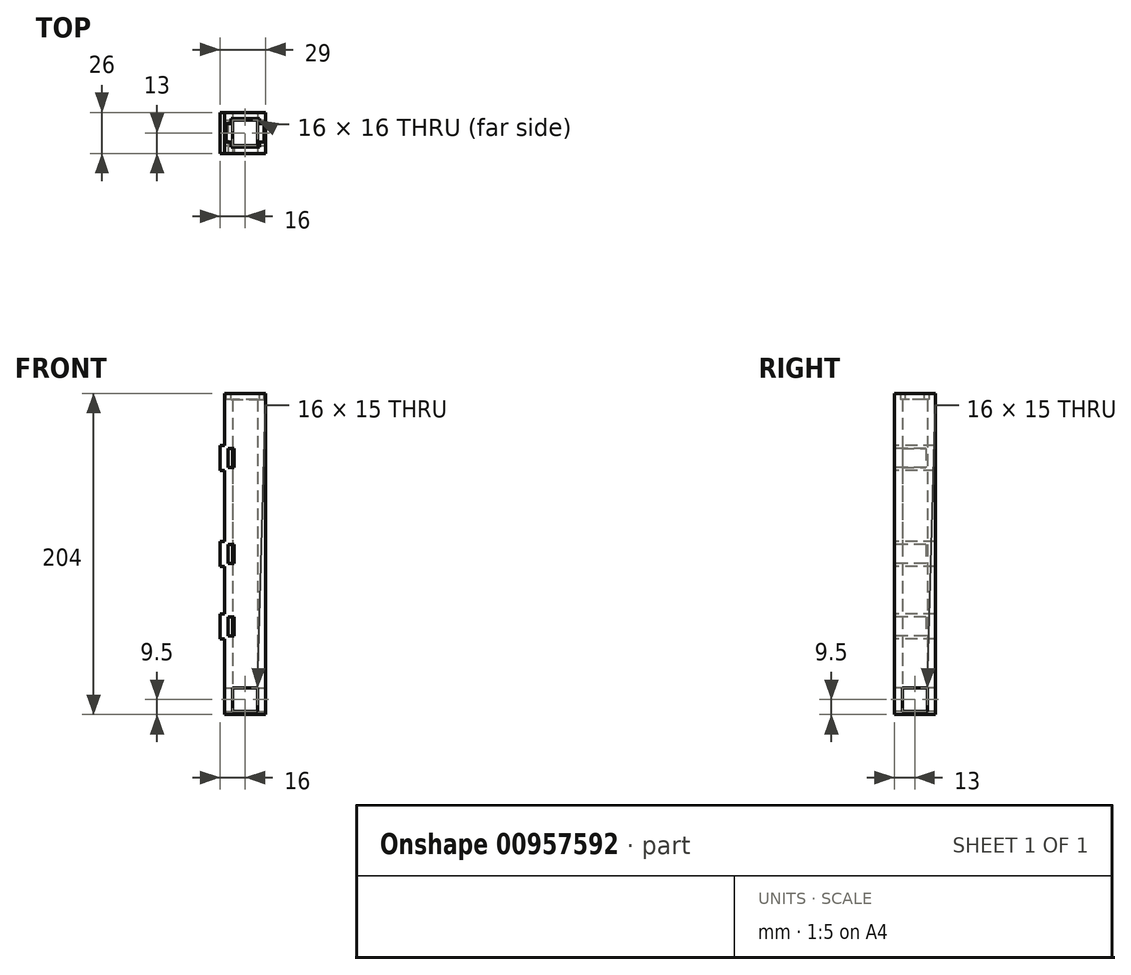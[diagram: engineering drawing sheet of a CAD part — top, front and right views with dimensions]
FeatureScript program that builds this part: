
annotation { "Feature Type Name" : "Feature", "Feature Type Description" : "" }
export const myFeature = defineFeature(function(context is Context, id is Id, definition is map)
    precondition{}
    {
        {
            var Q0;
            Q0=qCreatedBy(makeId("Top.planeOp"),FACE);
            var sketch = newSketch(context, id + "F0", { "sketchPlane" : qUnion([Q0])});
            skLineSegment(sketch, "E0.bottom", {"start": v(13, 13) * mm, "end": v(-13, 13) * mm});
            skLineSegment(sketch, "E0.top", {"start": v(13, -13) * mm, "end": v(-13, -13) * mm});
            skLineSegment(sketch, "E0.left", {"start": v(13, 13) * mm, "end": v(13, -13) * mm});
            skLineSegment(sketch, "E0.right", {"start": v(-13, 13) * mm, "end": v(-13, -13) * mm});
            skPoint(sketch, "E0.middle", {"position": v(0, 0) * mm});
            skLineSegment(sketch, "E1.bottom", {"start": v(8, 8) * mm, "end": v(-8, 8) * mm});
            skLineSegment(sketch, "E1.top", {"start": v(8, -8) * mm, "end": v(-8, -8) * mm});
            skLineSegment(sketch, "E1.left", {"start": v(8, 8) * mm, "end": v(8, -8) * mm});
            skLineSegment(sketch, "E1.right", {"start": v(-8, 8) * mm, "end": v(-8, -8) * mm});
            skSolve(sketch);
        }
        {
            var Q0;
            Q0=makeQuery(id+"F0.imprint","IMPRINT",FACE,{"disambiguationData":[TD([[makeQuery(id+"F0.imprint","IMPRINT",EDGE,{"derivedFrom":sQuery(id+"F0.wireOp",EDGE,"E0.bottom")}),1.0]])]});
            var Q1;
            Q1=makeQuery(id+"F0.imprint","IMPRINT",FACE,{"disambiguationData":[TD([[makeQuery(id+"F0.imprint","IMPRINT",EDGE,{"derivedFrom":sQuery(id+"F0.wireOp",EDGE,"E1.bottom")}),-1.0]])]});
            var Q2;
            Q2=makeQuery(id+"F0.imprint","IMPRINT",FACE,{"disambiguationData":[TD([[makeQuery(id+"F0.imprint","IMPRINT",EDGE,{"derivedFrom":sQuery(id+"F0.wireOp",EDGE,"E1.bottom")}),1.0]])]});
            extrude(context, id + "F1", {"entities" : qUnion([Q0, Q1, Q2]), "depth" : 2 * mm, "offsetDistance" : 25 * mm});
        }
        {
            var Q0;
            Q0=qSketchRegion(id+"F0",true);
            var Q1;
            Q1=makeQuery(id+"F0.imprint","IMPRINT",FACE,{"disambiguationData":[TD([[makeQuery(id+"F0.imprint","IMPRINT",EDGE,{"derivedFrom":sQuery(id+"F0.wireOp",EDGE,"E1.bottom")}),-1.0]])]});
            extrude(context, id + "F2", {"entities" : qUnion([Q0, Q1]), "operationType" : NewBodyOperationType.ADD, "depth" : 200 * mm, "offsetDistance" : 25 * mm});
        }
        {
            var Q0;
            Q0=makeQuery(id+"F2.opExtrude","CAP_FACE",FACE,{"disambiguationData":[OSD([sQuery(id+"F0.wireOp",EDGE,"E0.bottom"),sQuery(id+"F0.wireOp",EDGE,"E0.top"),sQuery(id+"F0.wireOp",EDGE,"E0.left"),sQuery(id+"F0.wireOp",EDGE,"E0.right"),sQuery(id+"F0.wireOp",EDGE,"E1.bottom"),sQuery(id+"F0.wireOp",EDGE,"E1.top"),sQuery(id+"F0.wireOp",EDGE,"E1.left"),sQuery(id+"F0.wireOp",EDGE,"E1.right")])],"isStart":false});
            var sketch = newSketch(context, id + "F3", { "sketchPlane" : qUnion([Q0])});
            skLineSegment(sketch, "E2.bottom", {"start": v(-9, 9) * mm, "end": v(9, 9) * mm});
            skLineSegment(sketch, "E2.top", {"start": v(-9, -9) * mm, "end": v(9, -9) * mm});
            skLineSegment(sketch, "E2.left", {"start": v(-9, 9) * mm, "end": v(-9, -9) * mm});
            skLineSegment(sketch, "E2.right", {"start": v(9, 9) * mm, "end": v(9, -9) * mm});
            skPoint(sketch, "E2.middle", {"position": v(0, 0) * mm});
            skSolve(sketch);
        }
        {
            var Q0;
            Q0=makeQuery(id+"F3.imprint","IMPRINT",FACE,{"disambiguationData":[TD([[makeQuery(id+"F3.imprint","IMPRINT",EDGE,{"derivedFrom":sQuery(id+"F3.wireOp",EDGE,"E2.bottom")}),1.0]])]});
            extrude(context, id + "F4", {"entities" : qUnion([Q0]), "operationType" : NewBodyOperationType.ADD, "depth" : 4 * mm, "offsetDistance" : 25 * mm});
        }
        {
            var Q0;
            {var subQ0=sQuery(id+"F0.wireOp",EDGE,"E0.left");Q0=makeQuery(id+"F4.boolean.opBoolean","MERGE",FACE,{"derivedFrom":[makeQuery(id+"F2.boolean.opBoolean","MERGE",FACE,{"derivedFrom":[makeQuery(id+"F1.opExtrude","SWEPT_FACE",FACE,{"disambiguationData":[OSD([subQ0])]}),makeQuery(id+"F2.opExtrude","SWEPT_FACE",FACE,{"disambiguationData":[OSD([subQ0])]})]}),makeQuery(id+"F4.opExtrude","SWEPT_FACE",FACE,{"disambiguationData":[OSD([subQ0])]})]});}
            var sketch = newSketch(context, id + "F5", { "sketchPlane" : qUnion([Q0])});
            skLineSegment(sketch, "E3.bottom", {"start": v(-7.98, 198) * mm, "end": v(8.02, 198) * mm});
            skLineSegment(sketch, "E3.top", {"start": v(-7.98, 2) * mm, "end": v(8.02, 2) * mm});
            skLineSegment(sketch, "E3.left", {"start": v(-7.98, 198) * mm, "end": v(-7.98, 2) * mm});
            skLineSegment(sketch, "E3.right", {"start": v(8.02, 198) * mm, "end": v(8.02, 2) * mm});
            skLineSegment(sketch, "E4", {"start": v(-7.98, 0) * mm, "end": v(-7.98, 200) * mm, "construction": true});
            skLineSegment(sketch, "E5", {"start": v(8.02, 0) * mm, "end": v(8.02, 200) * mm, "construction": true});
            skSolve(sketch);
        }
        {
            var Q0;
            Q0=makeQuery(id+"F0.imprint","IMPRINT",FACE,{"disambiguationData":[TD([[makeQuery(id+"F0.imprint","IMPRINT",EDGE,{"derivedFrom":sQuery(id+"F0.wireOp",EDGE,"E1.bottom")}),1.0]])]});
            extrude(context, id + "F6", {"entities" : qUnion([Q0]), "operationType" : NewBodyOperationType.REMOVE, "depth" : 25 * mm, "offsetDistance" : 25 * mm});
        }
        {
            var Q0;
            {var subQ0=sQuery(id+"F0.wireOp",EDGE,"E0.top");Q0=makeQuery(id+"F4.boolean.opBoolean","MERGE",FACE,{"derivedFrom":[makeQuery(id+"F2.boolean.opBoolean","MERGE",FACE,{"derivedFrom":[makeQuery(id+"F1.opExtrude","SWEPT_FACE",FACE,{"disambiguationData":[OSD([subQ0])]}),makeQuery(id+"F2.opExtrude","SWEPT_FACE",FACE,{"disambiguationData":[OSD([subQ0])]})]}),makeQuery(id+"F4.opExtrude","SWEPT_FACE",FACE,{"disambiguationData":[OSD([subQ0])]})]});}
            var sketch = newSketch(context, id + "F7", { "sketchPlane" : qUnion([Q0])});
            skLineSegment(sketch, "E6.bottom", {"start": v(-13, 155) * mm, "end": v(-16, 155) * mm});
            skLineSegment(sketch, "E6.top", {"start": v(-13, 171) * mm, "end": v(-16, 171) * mm});
            skLineSegment(sketch, "E6.left", {"start": v(-13, 171) * mm, "end": v(-13, 155) * mm});
            skLineSegment(sketch, "E6.right", {"start": v(-16, 171) * mm, "end": v(-16, 155) * mm});
            skLineSegment(sketch, "E7.bottom", {"start": v(-13, 110) * mm, "end": v(-16, 110) * mm});
            skLineSegment(sketch, "E7.top", {"start": v(-13, 94) * mm, "end": v(-16, 94) * mm});
            skLineSegment(sketch, "E7.left", {"start": v(-13, 110) * mm, "end": v(-13, 94) * mm});
            skLineSegment(sketch, "E7.right", {"start": v(-16, 110) * mm, "end": v(-16, 94) * mm});
            skLineSegment(sketch, "E8.bottom", {"start": v(-13, 64) * mm, "end": v(-16, 64) * mm});
            skLineSegment(sketch, "E8.top", {"start": v(-13, 48) * mm, "end": v(-16, 48) * mm});
            skLineSegment(sketch, "E8.left", {"start": v(-13, 64) * mm, "end": v(-13, 48) * mm});
            skLineSegment(sketch, "E8.right", {"start": v(-16, 64) * mm, "end": v(-16, 48) * mm});
            skSolve(sketch);
        }
        {
            var Q0;
            Q0 = qSketchRegion(id + "F7", true);
            extrude(context, id + "F8", {"entities" : qUnion([Q0]), "operationType" : NewBodyOperationType.ADD, "oppositeDirection" : true, "depth" : 26 * mm, "offsetDistance" : 25 * mm});
        }
        {
            var Q0;
            {var subQ0=sQuery(id+"F0.wireOp",EDGE,"E0.top");Q0=makeQuery(id+"F8.boolean.opBoolean","MERGE",FACE,{"derivedFrom":[makeQuery(id+"F4.boolean.opBoolean","MERGE",FACE,{"derivedFrom":[makeQuery(id+"F2.boolean.opBoolean","MERGE",FACE,{"derivedFrom":[makeQuery(id+"F1.opExtrude","SWEPT_FACE",FACE,{"disambiguationData":[OSD([subQ0])]}),makeQuery(id+"F2.opExtrude","SWEPT_FACE",FACE,{"disambiguationData":[OSD([subQ0])]})]}),makeQuery(id+"F4.opExtrude","SWEPT_FACE",FACE,{"disambiguationData":[OSD([subQ0])]})]}),makeQuery(id+"F8.opExtrude","CAP_FACE",FACE,{"disambiguationData":[OSD([sQuery(id+"F7.wireOp",EDGE,"E6.bottom"),sQuery(id+"F7.wireOp",EDGE,"E6.top"),sQuery(id+"F7.wireOp",EDGE,"E6.left"),sQuery(id+"F7.wireOp",EDGE,"E6.right")])],"isStart":true})]});}
            var sketch = newSketch(context, id + "F9", { "sketchPlane" : qUnion([Q0])});
            skLineSegment(sketch, "E9.bottom", {"start": v(-11, 169) * mm, "end": v(-7, 169) * mm});
            skLineSegment(sketch, "E9.top", {"start": v(-11, 157) * mm, "end": v(-7, 157) * mm});
            skLineSegment(sketch, "E9.left", {"start": v(-11, 169) * mm, "end": v(-11, 157) * mm});
            skLineSegment(sketch, "E9.right", {"start": v(-7, 169) * mm, "end": v(-7, 157) * mm});
            skSolve(sketch);
        }
        {
            var Q0;
            Q0 = qSketchRegion(id + "F9", true);
            extrude(context, id + "F10", {"entities" : qUnion([Q0]), "operationType" : NewBodyOperationType.REMOVE, "oppositeDirection" : true, "depth" : 20 * mm, "offsetDistance" : 25 * mm});
        }
        {
            var Q0;
            {var subQ0=sQuery(id+"F0.wireOp",EDGE,"E0.top");Q0=makeQuery(id+"F8.boolean.opBoolean","MERGE",FACE,{"derivedFrom":[makeQuery(id+"F4.boolean.opBoolean","MERGE",FACE,{"derivedFrom":[makeQuery(id+"F2.boolean.opBoolean","MERGE",FACE,{"derivedFrom":[makeQuery(id+"F1.opExtrude","SWEPT_FACE",FACE,{"disambiguationData":[OSD([subQ0])]}),makeQuery(id+"F2.opExtrude","SWEPT_FACE",FACE,{"disambiguationData":[OSD([subQ0])]})]}),makeQuery(id+"F4.opExtrude","SWEPT_FACE",FACE,{"disambiguationData":[OSD([subQ0])]})]}),makeQuery(id+"F8.opExtrude","CAP_FACE",FACE,{"disambiguationData":[OSD([sQuery(id+"F7.wireOp",EDGE,"E6.bottom"),sQuery(id+"F7.wireOp",EDGE,"E6.top"),sQuery(id+"F7.wireOp",EDGE,"E6.left"),sQuery(id+"F7.wireOp",EDGE,"E6.right")])],"isStart":true})]});}
            var sketch = newSketch(context, id + "F11", { "sketchPlane" : qUnion([Q0])});
            skLineSegment(sketch, "E10.bottom", {"start": v(-8, 2) * mm, "end": v(8, 2) * mm});
            skLineSegment(sketch, "E10.top", {"start": v(-8, 17) * mm, "end": v(8, 17) * mm});
            skLineSegment(sketch, "E10.left", {"start": v(-8, 2) * mm, "end": v(-8, 17) * mm});
            skLineSegment(sketch, "E10.right", {"start": v(8, 2) * mm, "end": v(8, 17) * mm});
            skSolve(sketch);
        }
        {
            var Q0;
            Q0 = qSketchRegion(id + "F11", true);
            extrude(context, id + "F12", {"entities" : qUnion([Q0]), "operationType" : NewBodyOperationType.REMOVE, "oppositeDirection" : true, "depth" : 40 * mm, "offsetDistance" : 25 * mm});
        }
        {
            var Q0;
            Q0=makeQuery(id+"F5.imprint","IMPRINT",FACE,{"disambiguationData":[TD([[makeQuery(id+"F5.imprint","IMPRINT",EDGE,{"derivedFrom":sQuery(id+"F5.wireOp",EDGE,"E3.bottom")}),-1.0]])]});
            var sketch = newSketch(context, id + "F13", { "sketchPlane" : qUnion([Q0])});
            skLineSegment(sketch, "E11.bottom", {"start": v(-8, 2) * mm, "end": v(8, 2) * mm});
            skLineSegment(sketch, "E11.top", {"start": v(-8, 17) * mm, "end": v(8, 17) * mm});
            skLineSegment(sketch, "E11.left", {"start": v(-8, 2) * mm, "end": v(-8, 17) * mm});
            skLineSegment(sketch, "E11.right", {"start": v(8, 2) * mm, "end": v(8, 17) * mm});
            skSolve(sketch);
        }
        {
            var Q0;
            Q0 = qSketchRegion(id + "F13", true);
            extrude(context, id + "F14", {"entities" : qUnion([Q0]), "operationType" : NewBodyOperationType.REMOVE, "oppositeDirection" : true, "depth" : 40 * mm, "offsetDistance" : 25 * mm});
        }
        {
            var Q0;
            {var subQ0=sQuery(id+"F0.wireOp",EDGE,"E0.top");Q0=makeQuery(id+"F8.boolean.opBoolean","MERGE",FACE,{"derivedFrom":[makeQuery(id+"F4.boolean.opBoolean","MERGE",FACE,{"derivedFrom":[makeQuery(id+"F2.boolean.opBoolean","MERGE",FACE,{"derivedFrom":[makeQuery(id+"F1.opExtrude","SWEPT_FACE",FACE,{"disambiguationData":[OSD([subQ0])]}),makeQuery(id+"F2.opExtrude","SWEPT_FACE",FACE,{"disambiguationData":[OSD([subQ0])]})]}),makeQuery(id+"F4.opExtrude","SWEPT_FACE",FACE,{"disambiguationData":[OSD([subQ0])]})]}),makeQuery(id+"F8.opExtrude","CAP_FACE",FACE,{"disambiguationData":[OSD([sQuery(id+"F7.wireOp",EDGE,"E6.bottom"),sQuery(id+"F7.wireOp",EDGE,"E6.top"),sQuery(id+"F7.wireOp",EDGE,"E6.left"),sQuery(id+"F7.wireOp",EDGE,"E6.right")])],"isStart":true})]});}
            var sketch = newSketch(context, id + "F15", { "sketchPlane" : qUnion([Q0])});
            skLineSegment(sketch, "E12.bottom", {"start": v(-7, 108) * mm, "end": v(-11, 108) * mm});
            skLineSegment(sketch, "E12.top", {"start": v(-7, 96) * mm, "end": v(-11, 96) * mm});
            skLineSegment(sketch, "E12.left", {"start": v(-7, 108) * mm, "end": v(-7, 96) * mm});
            skLineSegment(sketch, "E12.right", {"start": v(-11, 108) * mm, "end": v(-11, 96) * mm});
            skLineSegment(sketch, "E13.bottom", {"start": v(-7, 62) * mm, "end": v(-11, 62) * mm});
            skLineSegment(sketch, "E13.top", {"start": v(-7, 50) * mm, "end": v(-11, 50) * mm});
            skLineSegment(sketch, "E13.left", {"start": v(-7, 62) * mm, "end": v(-7, 50) * mm});
            skLineSegment(sketch, "E13.right", {"start": v(-11, 62) * mm, "end": v(-11, 50) * mm});
            skSolve(sketch);
        }
        {
            var Q0;
            Q0 = qSketchRegion(id + "F15", true);
            extrude(context, id + "F16", {"entities" : qUnion([Q0]), "operationType" : NewBodyOperationType.REMOVE, "oppositeDirection" : true, "depth" : 20 * mm, "offsetDistance" : 25 * mm});
        }
        {
            var Q0;
            Q0=makeQuery(id+"F4.opExtrude","CAP_FACE",FACE,{"disambiguationData":[OSD([sQuery(id+"F0.wireOp",EDGE,"E0.bottom"),sQuery(id+"F0.wireOp",EDGE,"E0.top"),sQuery(id+"F0.wireOp",EDGE,"E0.left"),sQuery(id+"F0.wireOp",EDGE,"E0.right"),sQuery(id+"F3.wireOp",EDGE,"E2.bottom"),sQuery(id+"F3.wireOp",EDGE,"E2.top"),sQuery(id+"F3.wireOp",EDGE,"E2.left"),sQuery(id+"F3.wireOp",EDGE,"E2.right")])],"isStart":false});
            var sketch = newSketch(context, id + "F17", { "sketchPlane" : qUnion([Q0])});
            skPoint(sketch, "E14.middle", {"position": v(0, 0) * mm});
            skLineSegment(sketch, "E15.bottom", {"start": v(-9, 6) * mm, "end": v(-12, 6) * mm});
            skLineSegment(sketch, "E15.top", {"start": v(-9, -6) * mm, "end": v(-12, -6) * mm});
            skLineSegment(sketch, "E15.left", {"start": v(-9, 6) * mm, "end": v(-9, -6) * mm});
            skLineSegment(sketch, "E15.right", {"start": v(-12, 6) * mm, "end": v(-12, -6) * mm});
            skLineSegment(sketch, "E16.bottom", {"start": v(9, 6) * mm, "end": v(12, 6) * mm});
            skLineSegment(sketch, "E16.top", {"start": v(9, -6) * mm, "end": v(12, -6) * mm});
            skLineSegment(sketch, "E16.left", {"start": v(9, 6) * mm, "end": v(9, -6) * mm});
            skLineSegment(sketch, "E16.right", {"start": v(12, 6) * mm, "end": v(12, -6) * mm});
            skSolve(sketch);
        }
        {
            var Q0;
            Q0 = qSketchRegion(id + "F17", true);
            extrude(context, id + "F18", {"entities" : qUnion([Q0]), "operationType" : NewBodyOperationType.REMOVE, "oppositeDirection" : true, "depth" : 4 * mm, "offsetDistance" : 25 * mm});
        }
    });
